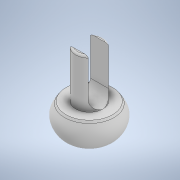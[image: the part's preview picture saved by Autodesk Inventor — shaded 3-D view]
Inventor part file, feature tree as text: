
AUTODESK INVENTOR PART (.ipt)
format: ipt  version: 2022 (Build 260153000, 153)  size: 188,928 bytes
history: native  units: mm
features: extrude x3, sketch x3, fillet x2, chamfer x1
ambient origin geometry x8: Origin, YZ Plane, XZ Plane, XY Plane, X Axis, Y Axis, Z Axis, Center Point
bodies: Solid1 (feature_tree)
feature tree (9):
  extrude  "Extrusion1"  Depth=3.0mm
  chamfer  "Chamfer1"  Distance=3.0mm
  extrude  "Extrusion2"  Depth=3.0mm
  fillet  "Fillet1"  Radius=5.0mm
  fillet  "Fillet2"  Radius=0.2mm
  extrude  "Extrusion3"  Depth=2.1mm
  sketch  "Sketch1"  dims[d0=4.8mm d1=8.8mm d2=3.0mm d3=0.0mm]
  sketch  "Sketch2"  dims[d4=2.0mm d5=3.0mm d6=45.0deg d7=2.8mm d8=5.0mm d9=0.0mm d10=0.2mm]
  sketch  "Sketch3"  dims[d11=1.8mm d12=2.1mm d13=0.0mm d14=0.0mm]
